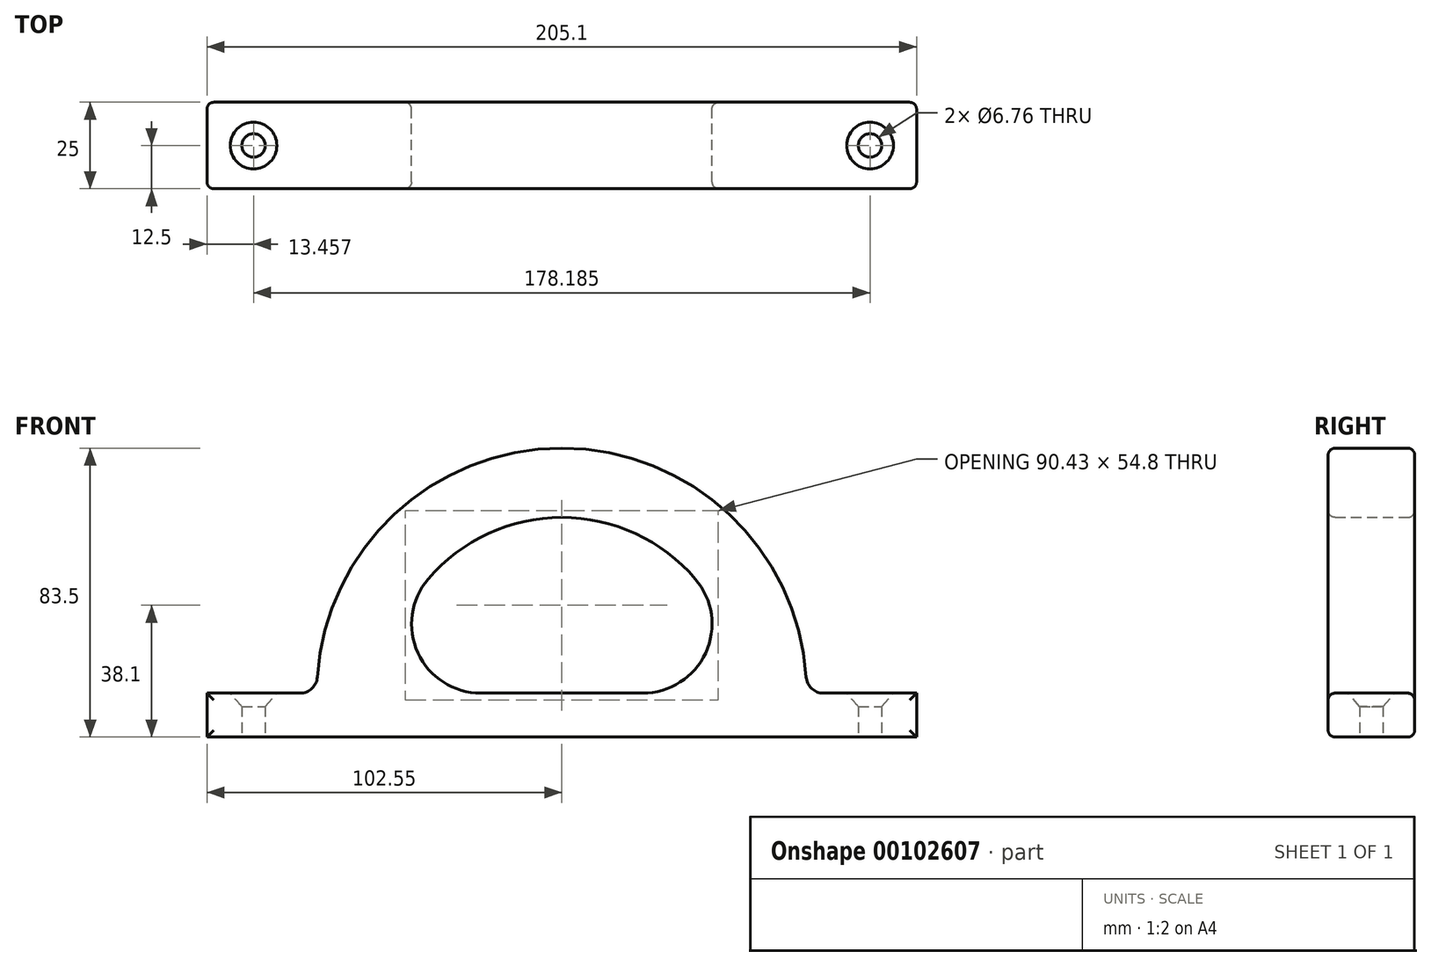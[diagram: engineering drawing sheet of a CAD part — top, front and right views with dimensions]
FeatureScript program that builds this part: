
annotation { "Feature Type Name" : "Feature", "Feature Type Description" : "" }
export const myFeature = defineFeature(function(context is Context, id is Id, definition is map)
    precondition{}
    {
        {
            var Q0;
            Q0=qCreatedBy(makeId("Front.planeOp"),FACE);
            var sketch = newSketch(context, id + "F0", { "sketchPlane" : qUnion([Q0])});
            skLineSegment(sketch, "E0.bottom", {"start": v(-102.55, 12.7) * mm, "end": v(102.55, 12.7) * mm});
            skLineSegment(sketch, "E0.top", {"start": v(-102.55, 0) * mm, "end": v(102.55, 0) * mm});
            skLineSegment(sketch, "E0.left", {"start": v(-102.55, 12.7) * mm, "end": v(-102.55, 0) * mm});
            skLineSegment(sketch, "E0.right", {"start": v(102.55, 12.7) * mm, "end": v(102.55, 0) * mm});
            skPoint(sketch, "E0.middle", {"position": v(0, 6.35) * mm});
            skArc(sketch, "E1", {"start": v(70.8, 12.7) * mm, "mid": v(0, 83.5) * mm, "end": v(-70.8, 12.7) * mm});
            skArc(sketch, "E2.0", {"start": v(50.8, 12.7) * mm, "mid": v(0, 63.5) * mm, "end": v(-50.8, 12.7) * mm});
            skSolve(sketch);
        }
        {
            var Q0;
            Q0 = qSketchRegion(id + "F0", true);
            extrude(context, id + "F1", {"entities" : qUnion([Q0]), "depth" : 25 * mm});
        }
        {
            var Q0;
            {var subQ0=sQuery(id+"F0.wireOp",EDGE,"E2.0");var subQ1=sQuery(id+"F0.wireOp",EDGE,"E0.bottom");Q0=makeQuery(id+"F1.opExtrude","SWEPT_EDGE",EDGE,{"disambiguationData":[OSD([subQ1,subQ0]),TDD([makeQuery(id+"F0.imprint","INTERSECT",VERTEX,{"disambiguationData":[OD(0.0)],"derivedFrom":[subQ1,subQ0]})])]});}
            var Q1;
            {var subQ0=sQuery(id+"F0.wireOp",EDGE,"E2.0");var subQ1=sQuery(id+"F0.wireOp",EDGE,"E0.bottom");Q1=makeQuery(id+"F1.opExtrude","SWEPT_EDGE",EDGE,{"disambiguationData":[OSD([subQ1,subQ0]),TDD([makeQuery(id+"F0.imprint","INTERSECT",VERTEX,{"disambiguationData":[OD(1.0)],"derivedFrom":[subQ1,subQ0]})])]});}
            fillet(context, id + "F2", {"entities" : qUnion([Q0, Q1]), "radius" : 20 * mm, "tangentPropagation" : true, "allowEdgeOverflow" : false});
        }
        {
            var Q0;
            {var subQ0=sQuery(id+"F0.wireOp",EDGE,"E1");var subQ1=sQuery(id+"F0.wireOp",EDGE,"E0.bottom");Q0=makeQuery(id+"F1.opExtrude","SWEPT_EDGE",EDGE,{"disambiguationData":[OSD([subQ1,subQ0]),TDD([makeQuery(id+"F0.imprint","INTERSECT",VERTEX,{"disambiguationData":[OD(0.0)],"derivedFrom":[subQ1,subQ0]})])]});}
            var Q1;
            {var subQ0=sQuery(id+"F0.wireOp",EDGE,"E1");var subQ1=sQuery(id+"F0.wireOp",EDGE,"E0.bottom");Q1=makeQuery(id+"F1.opExtrude","SWEPT_EDGE",EDGE,{"disambiguationData":[OSD([subQ1,subQ0]),TDD([makeQuery(id+"F0.imprint","INTERSECT",VERTEX,{"disambiguationData":[OD(1.0)],"derivedFrom":[subQ1,subQ0]})])]});}
            fillet(context, id + "F3", {"entities" : qUnion([Q0, Q1]), "radius" : 5 * mm, "tangentPropagation" : true, "allowEdgeOverflow" : false});
        }
        {
            var Q0;
            {var subQ0=sQuery(id+"F0.wireOp",EDGE,"E0.bottom");Q0=makeQuery(id+"F1.opExtrude","SWEPT_FACE",FACE,{"disambiguationData":[OSD([subQ0]),TDD([makeQuery(id+"F0.imprint","IMPRINT",EDGE,{"disambiguationData":[TD([[makeQuery(id+"F0.imprint","INTERSECT",VERTEX,{"derivedFrom":[subQ0,sQuery(id+"F0.wireOp",EDGE,"E0.right")]}),1.0]])],"derivedFrom":subQ0})])]});}
            var sketch = newSketch(context, id + "F4", { "sketchPlane" : qUnion([Q0])});
            skLineSegment(sketch, "E3", {"start": v(102.55, -12.5) * mm, "end": v(75.63, -12.5) * mm, "construction": true});
            skLineSegment(sketch, "E4", {"start": v(-102.55, -12.5) * mm, "end": v(-75.63, -12.5) * mm, "construction": true});
            skPoint(sketch, "E5", {"position": v(-89.1, -12.5) * mm});
            skPoint(sketch, "E6", {"position": v(89.1, -12.5) * mm});
            skSolve(sketch);
        }
        {
            var Q0;
            Q0=sQuery(id+"F4.wireOp",VERTEX,"E6");
            var Q1;
            Q1=sQuery(id+"F4.wireOp",VERTEX,"E5");
            var Q2;
            Q2=makeQuery(id+"F1.opExtrude","SWEPT_BODY",BODY,{"disambiguationData":[OSD([sQuery(id+"F0.wireOp",EDGE,"E0.bottom"),sQuery(id+"F0.wireOp",EDGE,"E0.top"),sQuery(id+"F0.wireOp",EDGE,"E0.left"),sQuery(id+"F0.wireOp",EDGE,"E0.right"),sQuery(id+"F0.wireOp",EDGE,"E1"),sQuery(id+"F0.wireOp",EDGE,"E2.0")])]});
            hole(context, id + "F5", {"style" : HoleStyle.C_SINK, "endStyle" : HoleEndStyle.BLIND, "standardTappedOrClearance" : lookupTablePath({ "standard" : "ANSI", "fit" : "Normal (ASME)", "size" : "1/4", "type" : "Clearance" }), "standardBlindInLast" : lookupTablePath({ "fit" : "Free", "standard" : "ANSI", "size" : "1/4", "type" : "Clearance" }), "holeDiameter" : 6.76 * mm, "cSinkDiameter" : 13.5 * mm, "cSinkAngle" : 82 * degree, "holeDepth" : 15 * mm, "locations" : qUnion([Q0, Q1]), "scope" : qUnion([Q2]), "startStyle" : HoleStartStyle.PART});
        }
        {
            var Q0;
            Q0=makeQuery(id+"F1.opExtrude","CAP_FACE",FACE,{"disambiguationData":[OSD([sQuery(id+"F0.wireOp",EDGE,"E0.bottom"),sQuery(id+"F0.wireOp",EDGE,"E0.top"),sQuery(id+"F0.wireOp",EDGE,"E0.left"),sQuery(id+"F0.wireOp",EDGE,"E0.right"),sQuery(id+"F0.wireOp",EDGE,"E1"),sQuery(id+"F0.wireOp",EDGE,"E2.0")])],"isStart":false});
            var Q1;
            Q1=makeQuery(id+"F1.opExtrude","CAP_FACE",FACE,{"disambiguationData":[OSD([sQuery(id+"F0.wireOp",EDGE,"E0.bottom"),sQuery(id+"F0.wireOp",EDGE,"E0.top"),sQuery(id+"F0.wireOp",EDGE,"E0.left"),sQuery(id+"F0.wireOp",EDGE,"E0.right"),sQuery(id+"F0.wireOp",EDGE,"E1"),sQuery(id+"F0.wireOp",EDGE,"E2.0")])],"isStart":true});
            fillet(context, id + "F6", {"entities" : qUnion([Q0, Q1]), "radius" : 2 * mm, "tangentPropagation" : true, "allowEdgeOverflow" : false});
        }
    });
